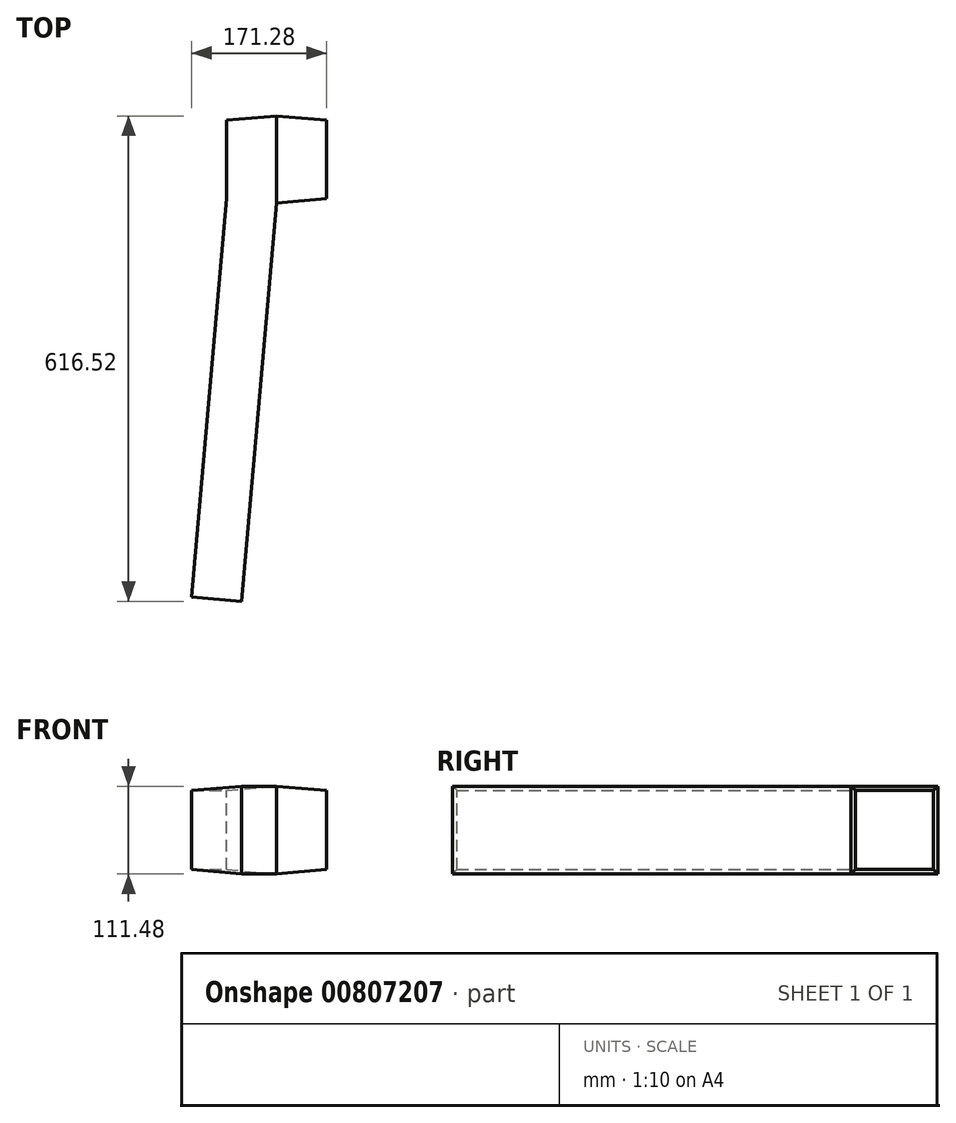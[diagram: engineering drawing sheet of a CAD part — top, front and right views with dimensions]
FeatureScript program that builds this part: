
annotation { "Feature Type Name" : "Feature", "Feature Type Description" : "" }
export const myFeature = defineFeature(function(context is Context, id is Id, definition is map)
    precondition{}
    {
        {
            var Q0;
            Q0=qCreatedBy(makeId("Right.planeOp"),FACE);
            var sketch = newSketch(context, id + "F0", { "sketchPlane" : qUnion([Q0])});
            skLineSegment(sketch, "E0.bottom", {"start": v(-196.93, -99.33) * mm, "end": v(-87.97, -99.33) * mm});
            skLineSegment(sketch, "E0.top", {"start": v(-196.93, 22.17) * mm, "end": v(-87.97, 22.17) * mm});
            skLineSegment(sketch, "E0.left", {"start": v(-196.93, -99.33) * mm, "end": v(-196.93, 22.17) * mm});
            skLineSegment(sketch, "E0.right", {"start": v(-87.97, -99.33) * mm, "end": v(-87.97, 22.17) * mm});
            skLineSegment(sketch, "E1.bottom", {"start": v(-4.63, 121.25) * mm, "end": v(105.82, 121.25) * mm});
            skLineSegment(sketch, "E1.top", {"start": v(-4.63, 9.77) * mm, "end": v(105.82, 9.77) * mm});
            skLineSegment(sketch, "E1.left", {"start": v(-4.63, 121.25) * mm, "end": v(-4.63, 9.77) * mm});
            skLineSegment(sketch, "E1.right", {"start": v(105.82, 121.25) * mm, "end": v(105.82, 9.77) * mm});
            skLineSegment(sketch, "E2.bottom", {"start": v(23.36, 55.75) * mm, "end": v(-64.3, 55.75) * mm});
            skLineSegment(sketch, "E2.top", {"start": v(23.36, -56.6) * mm, "end": v(-64.3, -56.6) * mm});
            skLineSegment(sketch, "E2.left", {"start": v(23.36, 55.75) * mm, "end": v(23.36, -56.6) * mm});
            skLineSegment(sketch, "E2.right", {"start": v(-64.3, 55.75) * mm, "end": v(-64.3, -56.6) * mm});
            skSolve(sketch);
        }
        {
            var Q0;
            {var subQ1=sQuery(id+"F0.wireOp",EDGE,"E1.bottom");Q0=makeQuery(id+"F0.imprint","IMPRINT",FACE,{"disambiguationData":[TD([[makeQuery(id+"F0.imprint","IMPRINT",EDGE,{"derivedFrom":subQ1}),-1.0]])]});}
            var Q1;
            {var subQ0=sQuery(id+"F0.wireOp",EDGE,"E1.left");var subQ1=sQuery(id+"F0.wireOp",EDGE,"E1.top");var subQ2=makeQuery(id+"F0.imprint","INTERSECT",VERTEX,{"derivedFrom":[subQ1,subQ0]});Q1=makeQuery(id+"F0.imprint","IMPRINT",FACE,{"disambiguationData":[TD([[makeQuery(id+"F0.imprint","IMPRINT",EDGE,{"disambiguationData":[TD([[subQ2,-1.0]])],"derivedFrom":subQ1}),1.0]])]});}
            extrude(context, id + "F1", {"entities" : qUnion([Q0, Q1]), "endBound" : BoundingType.SYMMETRIC, "depth" : 127 * mm, "offsetDistance" : 25.4 * mm, "hasDraft" : true, "draftAngle" : 5 * degree, "draftPullDirection" : true, "hasSecondDirection" : true, "secondDirectionOppositeDirection" : false, "secondDirectionDepth" : 101.6 * mm});
        }
        {
            var Q0;
            Q0=makeQuery(id+"F1.*.split.splitOp","SPLIT",FACE,{"derivedFrom":makeQuery(id+"F1.opExtrude","SWEPT_FACE",FACE,{"disambiguationData":[OSD([sQuery(id+"F0.wireOp",EDGE,"E1.left")])]}),"isFromBackBody":true});
            extrude(context, id + "F2", {"entities" : qUnion([Q0]), "operationType" : NewBodyOperationType.ADD, "depth" : 508 * mm, "offsetDistance" : 25.4 * mm});
        }
    });
